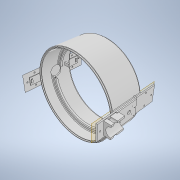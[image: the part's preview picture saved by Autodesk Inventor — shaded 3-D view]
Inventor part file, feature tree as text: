
AUTODESK INVENTOR PART (.ipt)
format: ipt  version: 2020.2 (Build 242310000, 310)  size: 670,720 bytes
history: native  units: mm
features: reference x25, extrude x24, sketch x24, other x7, plane x5, chamfer x2, pattern_circular x2, mirror x1
ambient origin geometry x8: Origin, YZ Plane, XZ Plane, XY Plane, X Axis, Y Axis, Z Axis, Center Point
bodies: Solid1 (feature_tree)
feature tree (90):
  extrude  "Extrusion1"  Depth=205.0mm
  extrude  "Extrusion2"  Depth=208.433333mm
  plane  "Work Plane4"
  extrude  "Extrusion3"  Depth=3.0mm TaperAngle=0.0deg
  extrude  "Extrusion4"  Depth=45.0mm
  extrude  "Extrusion6"  TaperAngle=0.0deg  [1 undecoded]
  extrude  "Extrusion8"  Depth=0.1mm
  chamfer  "Chamfer1"  Distance=20.0mm Angle=360.0deg
  pattern_circular  "Circular Pattern1"  Count=8  [1 undecoded]
  mirror  "Mirror1"
  plane  "Work Plane6"
  plane  "Work Plane8"
  extrude  "Extrusion15"  Depth=20.5mm
  extrude  "Extrusion16"  Depth=1.0mm
  extrude  "Extrusion17"  Depth=8.0mm
  extrude  "Extrusion20"  Depth=20.0mm TaperAngle=0.0deg
  chamfer  "Chamfer2"  Distance=5.0mm
  pattern_circular  "Circular Pattern2"  Count=2 Angle=360.0deg
  extrude  "Extrusion19"  Depth=191.666667mm
  extrude  "Extrusion21"  Depth=3.0mm TaperAngle=0.0deg
  extrude  "Extrusion22"  Depth=20.0mm
  extrude  "Extrusion23"  Depth=5.0mm
  extrude  "Extrusion24"  Depth=5.0mm
  plane  "Work Plane10"
  extrude  "Extrusion25"  Depth=5.0mm
  extrude  "Extrusion26"  Depth=5.0mm
  extrude  "Extrusion27"  TaperAngle=0.0deg  [1 undecoded]
  extrude  "Extrusion28"  TaperAngle=0.0deg  [1 undecoded]
  extrude  "Extrusion29"  TaperAngle=0.0deg  [1 undecoded]
  extrude  "Extrusion30"  Depth=5.0mm
  extrude  "Extrusion31"  Depth=5.0mm TaperAngle=0.0deg
  extrude  "Extrusion32"  Depth=5.0mm TaperAngle=0.0deg
  extrude  "Extrusion33"  Depth=5.0mm TaperAngle=0.0deg
  sketch  "Sketch1"  dims[d0=215.0mm d1=205.0mm]
  sketch  "Sketch2"  dims[d2=40.0mm d3=0.0mm d4=208.433333mm]
  plane  "Work Plane3"
  sketch  "Sketch4"  dims[d5=211.566667mm d6=3.0mm d7=0.0mm]
  sketch  "Sketch5"  dims[d8=45.0mm d9=45.0mm]
  reference  "Reference1"
  sketch  "Sketch6"  dims[d10=3.0mm d11=0.0mm d12=0.0mm]
  sketch  "Sketch8"  dims[d13=2.0mm d14=0.0mm d17=0.1mm]
  reference  "Reference7"
  reference  "Reference8"
  reference  "Reference9"
  reference  "Reference10"
  sketch  "Sketch16"  dims[d18=1.9mm]
  sketch  "Sketch17"  dims[d19=0.0mm d23=20.0mm d24=360.0deg]
  reference  "Reference12"
  reference  "Reference13"
  sketch  "Sketch18"  dims[d26=0.1mm]
  sketch  "Sketch20"  dims[d27=1.0mm d28=0.0mm]
  sketch  "Sketch21"  dims[d29=2.0mm d30=2.0mm d31=45.0deg]
  sketch  "Sketch22"  dims[d67=30.2mm]
  sketch  "Sketch23"  dims[d68=41.0mm d69=80.0mm]
  reference  "Reference14"
  reference  "Reference15"
  sketch  "Sketch24"  dims[d70=40.0mm d71=20.5mm]
  sketch  "Sketch25"  dims[d72=215.0mm d73=0.0mm d74=1.0mm]
  reference  "Reference16"
  reference  "Reference17"
  sketch  "Sketch26"  dims[d75=4.0mm d76=8.0mm]
  reference  "Reference18"
  reference  "Reference19"
  sketch  "Sketch27"  dims[d77=26.0mm d78=20.0mm d79=0.0mm]
  reference  "Reference20"
  reference  "Reference21"
  sketch  "Sketch28"  dims[d80=10.0mm d83=5.0mm d84=0.0mm]
  sketch  "Sketch29"  dims[d85=0.0mm]
  reference  "Reference22"
  reference  "Reference23"
  reference  "Reference24"
  reference  "Reference25"
  sketch  "Sketch30"  dims[d86=2.5mm d87=0.0mm d97=20.0mm d98=360.0deg]
  reference  "Reference26"
  reference  "Reference27"
  sketch  "Sketch31"  dims[d100=215.0mm d101=0.0mm d102=191.666667mm]
  sketch  "Sketch32"  dims[d103=198.333333mm d104=3.0mm d105=0.0mm]
  reference  "Reference28"
  reference  "Reference29"
  sketch  "Sketch33"  dims[d106=2.0mm d107=2.0mm d108=45.0deg d110=20.0mm]
  reference  "Reference30"
  sketch  "Sketch34"  dims[d111=72.5mm d112=0.0mm d114=0.4mm d115=6.0mm d116=6.8mm d117=6.8mm d118=0.0mm d119=0.0mm d120=0.0mm d121=6.0mm d122=4.0mm d123=0.0mm d124=7.5mm d125=0.0mm d126=3.0mm d127=0.0mm d128=2.0mm d129=2.0mm d130=6.0mm d131=0.0mm d132=-7.0mm d133=16.0mm d134=8.0mm d135=0.5mm d136=40.0mm d137=30.2mm d138=3.0mm d139=22.0mm d140=0.0mm d141=2.0mm d142=2.0mm d143=10.0mm d144=0.0mm d145=5.0mm d146=5.0mm d147=4.0mm d148=0.0mm d149=100.0mm d150=0.0mm d151=57.0mm d153=10.0mm d154=3.0mm d155=0.0mm d156=10.0mm d157=0.0mm d158=3.0mm d159=3.0mm d160=5.0mm d161=0.0mm d162=1.5mm d163=0.0mm d164=2.0mm d165=2.0mm d166=5.0mm d167=0.0mm d168=5.0mm d169=17.0mm d170=0.0mm d171=0.4mm d172=17.5mm d173=0.0mm d174=3.0mm d175=3.0mm d88=0.872665mm]
  reference  "Reference31"
  other  "<userpath>\OneDrive\Apps\0011_VentControlValve\Assembly.iam"
  other  "Assembly.iam"
  other  "Base:1"
  other  "Butterfly Valve:1"
  other  "limitSwitch:2"
  other  "limitSwitch:1"
  other  "motor+Gearbox:1"
note: 5 required parameter values undecoded (feature->parameter linkage not recoverable at this tier; creation-order binding heuristic only, values carry confidence <= 0.55)
